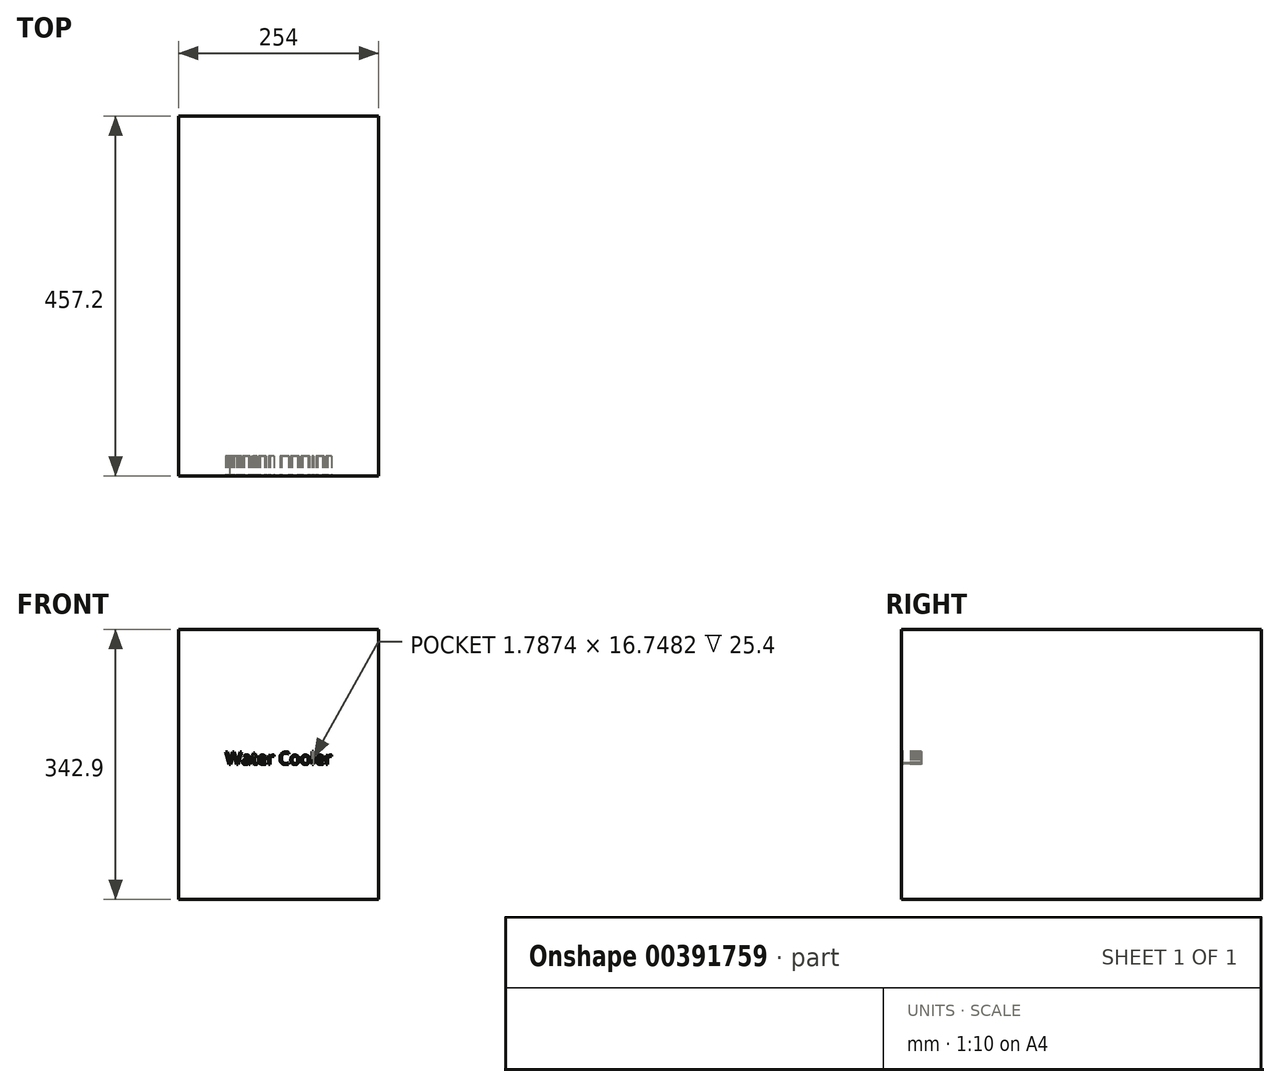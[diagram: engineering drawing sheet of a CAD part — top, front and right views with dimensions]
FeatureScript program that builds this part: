
annotation { "Feature Type Name" : "Feature", "Feature Type Description" : "" }
export const myFeature = defineFeature(function(context is Context, id is Id, definition is map)
    precondition{}
    {
        {
            var Q0;
            Q0=qCreatedBy(makeId("Front.planeOp"),FACE);
            var sketch = newSketch(context, id + "F0", { "sketchPlane" : qUnion([Q0])});
            skLineSegment(sketch, "E0.bottom", {"start": v(127, 171.45) * mm, "end": v(-127, 171.45) * mm});
            skLineSegment(sketch, "E0.top", {"start": v(127, -171.45) * mm, "end": v(-127, -171.45) * mm});
            skLineSegment(sketch, "E0.left", {"start": v(127, 171.45) * mm, "end": v(127, -171.45) * mm});
            skLineSegment(sketch, "E0.right", {"start": v(-127, 171.45) * mm, "end": v(-127, -171.45) * mm});
            skPoint(sketch, "E0.middle", {"position": v(0, 0) * mm});
            skSolve(sketch);
        }
        {
            var Q0;
            Q0=makeQuery(id+"F0.imprint","IMPRINT",FACE,{"disambiguationData":[TD([[makeQuery(id+"F0.imprint","IMPRINT",EDGE,{"derivedFrom":sQuery(id+"F0.wireOp",EDGE,"E0.bottom")}),1.0]])]});
            extrude(context, id + "F1", {"entities" : qUnion([Q0]), "oppositeDirection" : true, "depth" : 457.2 * mm});
        }
        {
            var Q0;
            Q0=makeQuery(id+"F1.opExtrude","CAP_FACE",FACE,{"disambiguationData":[OSD([sQuery(id+"F0.wireOp",EDGE,"E0.bottom"),sQuery(id+"F0.wireOp",EDGE,"E0.top"),sQuery(id+"F0.wireOp",EDGE,"E0.left"),sQuery(id+"F0.wireOp",EDGE,"E0.right")])],"isStart":true});
            var sketch = newSketch(context, id + "F2", { "sketchPlane" : qUnion([Q0])});
            skText(sketch, "E1", { "text": "Water Cooler", "fontName": "OpenSans-Regular.ttf"});
            const initialGuessF2  = {"E1": [-0.06732, 0, 1, 0, 0.01587]};
            skSetInitialGuess(sketch, initialGuessF2);
            skSolve(sketch);
        }
        {
            var Q0;
            Q0=qSketchRegion(id+"F2",true);
            extrude(context, id + "F3", {"entities" : qUnion([Q0]), "operationType" : NewBodyOperationType.REMOVE, "oppositeDirection" : true, "depth" : 25.4 * mm});
        }
    });
